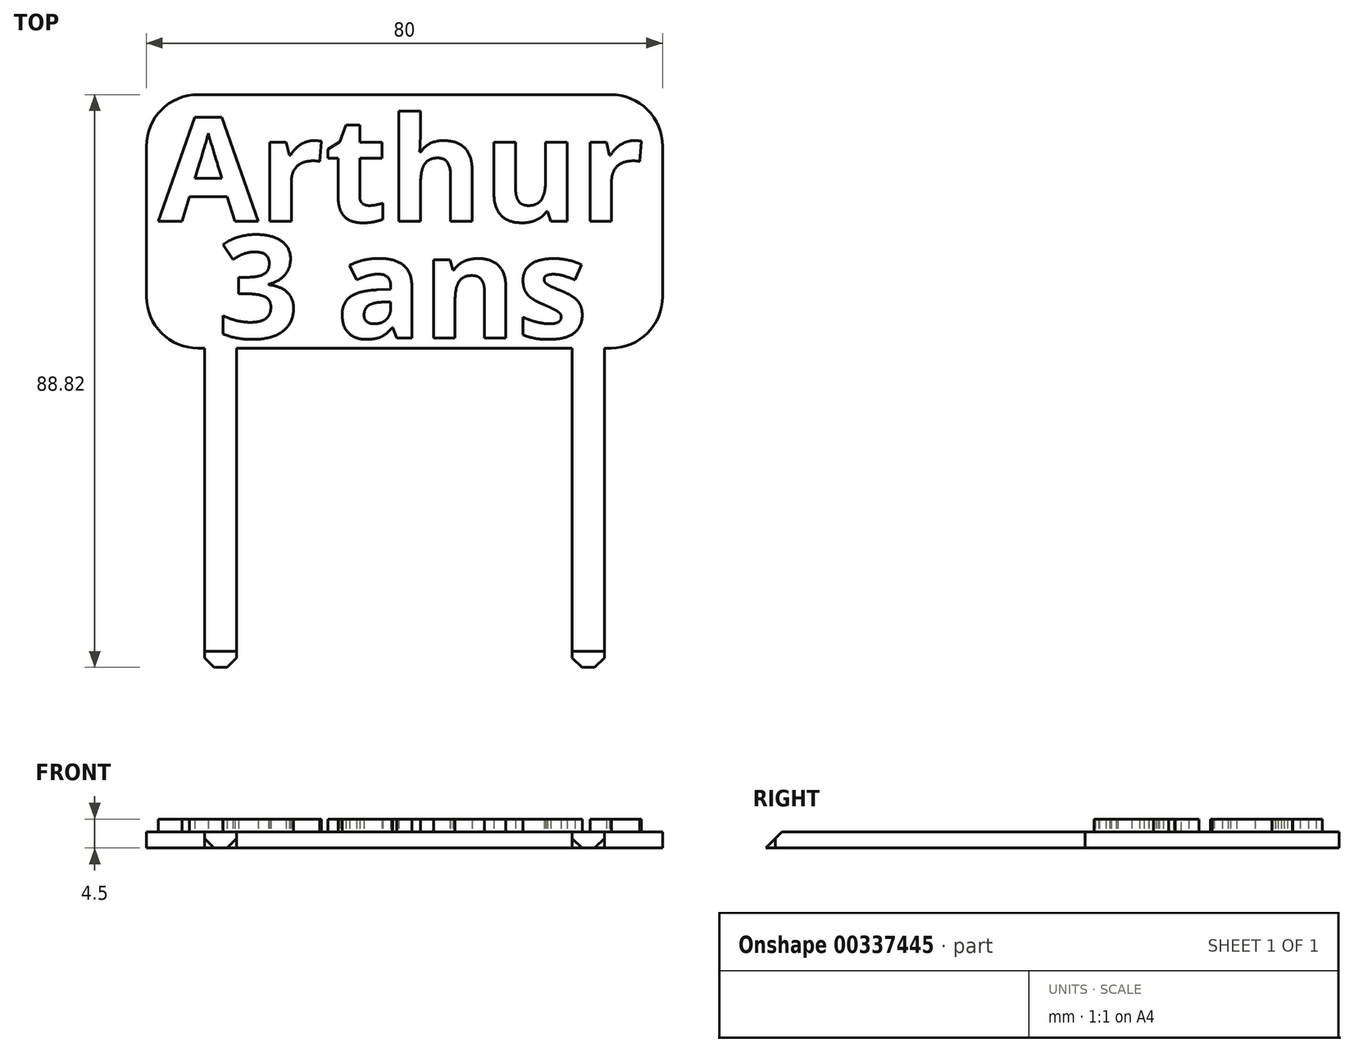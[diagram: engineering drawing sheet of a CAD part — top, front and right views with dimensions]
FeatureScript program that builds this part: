
annotation { "Feature Type Name" : "Feature", "Feature Type Description" : "" }
export const myFeature = defineFeature(function(context is Context, id is Id, definition is map)
    precondition{}
    {
        {
            var Q0;
            Q0=qCreatedBy(makeId("Top.planeOp"),FACE);
            var sketch = newSketch(context, id + "F0", { "sketchPlane" : qUnion([Q0])});
            skLineSegment(sketch, "E0.bottom", {"start": v(-40, 19.66) * mm, "end": v(40, 19.66) * mm});
            skLineSegment(sketch, "E0.top", {"start": v(-40, -19.66) * mm, "end": v(40, -19.66) * mm});
            skLineSegment(sketch, "E0.left", {"start": v(-40, 19.66) * mm, "end": v(-40, -19.66) * mm});
            skLineSegment(sketch, "E0.right", {"start": v(40, 19.66) * mm, "end": v(40, -19.66) * mm});
            skSolve(sketch);
        }
        {
            var Q0;
            Q0 = qSketchRegion(id + "F0", true);
            extrude(context, id + "F1", {"entities" : qUnion([Q0]), "depth" : 2.5 * mm});
        }
        {
            var Q0;
            Q0=makeQuery(id+"F1.opExtrude","CAP_FACE",FACE,{"disambiguationData":[OSD([sQuery(id+"F0.wireOp",EDGE,"E0.bottom"),sQuery(id+"F0.wireOp",EDGE,"E0.top"),sQuery(id+"F0.wireOp",EDGE,"E0.left"),sQuery(id+"F0.wireOp",EDGE,"E0.right")])],"isStart":false});
            var sketch = newSketch(context, id + "F2", { "sketchPlane" : qUnion([Q0])});
            skText(sketch, "E1", { "text": "Arthur", "fontName": "OpenSans-Bold.ttf"});
            skText(sketch, "E2", { "text": "3 ans", "fontName": "OpenSans-Bold.ttf"});
            const initialGuessF2  = {"E1": [-0.03818, 0, 1, 0, 0.01622], "E2": [-0.029, -0.01808, 1, 0, 0.01596]};
            skSetInitialGuess(sketch, initialGuessF2);
            skSolve(sketch);
        }
        {
            var Q0;
            Q0 = qSketchRegion(id + "F2", true);
            extrude(context, id + "F3", {"entities" : qUnion([Q0]), "operationType" : NewBodyOperationType.ADD, "depth" : 2 * mm});
        }
        {
            var Q0;
            Q0=qCreatedBy(makeId("Top.planeOp"),FACE);
            var sketch = newSketch(context, id + "F4", { "sketchPlane" : qUnion([Q0])});
            skLineSegment(sketch, "E3.bottom", {"start": v(-31, -69.66) * mm, "end": v(-26, -69.66) * mm});
            skLineSegment(sketch, "E3.top", {"start": v(-31, -19.66) * mm, "end": v(-26, -19.66) * mm});
            skLineSegment(sketch, "E3.left", {"start": v(-31, -69.66) * mm, "end": v(-31, -19.66) * mm});
            skLineSegment(sketch, "E3.right", {"start": v(-26, -69.66) * mm, "end": v(-26, -19.66) * mm});
            skLineSegment(sketch, "E4.MirrorCS", {"start": v(26, -69.66) * mm, "end": v(26, -19.66) * mm});
            skLineSegment(sketch, "E5.MirrorCS", {"start": v(31, -69.66) * mm, "end": v(26, -69.66) * mm});
            skLineSegment(sketch, "E6.MirrorCS", {"start": v(31, -69.66) * mm, "end": v(31, -19.66) * mm});
            skLineSegment(sketch, "E7.MirrorCS", {"start": v(31, -19.66) * mm, "end": v(26, -19.66) * mm});
            skSolve(sketch);
        }
        {
            var Q0;
            Q0 = qSketchRegion(id + "F4", true);
            extrude(context, id + "F5", {"entities" : qUnion([Q0]), "operationType" : NewBodyOperationType.ADD, "depth" : 2.5 * mm});
        }
        {
            var Q0;
            Q0=makeQuery(id+"F1.opExtrude","SWEPT_EDGE",EDGE,{"disambiguationData":[OSD([sQuery(id+"F0.wireOp",EDGE,"E0.top"),sQuery(id+"F0.wireOp",EDGE,"E0.right")])]});
            var Q1;
            Q1=makeQuery(id+"F1.opExtrude","SWEPT_EDGE",EDGE,{"disambiguationData":[OSD([sQuery(id+"F0.wireOp",EDGE,"E0.bottom"),sQuery(id+"F0.wireOp",EDGE,"E0.right")])]});
            var Q2;
            Q2=makeQuery(id+"F1.opExtrude","SWEPT_EDGE",EDGE,{"disambiguationData":[OSD([sQuery(id+"F0.wireOp",EDGE,"E0.top"),sQuery(id+"F0.wireOp",EDGE,"E0.left")])]});
            var Q3;
            Q3=makeQuery(id+"F1.opExtrude","SWEPT_EDGE",EDGE,{"disambiguationData":[OSD([sQuery(id+"F0.wireOp",EDGE,"E0.bottom"),sQuery(id+"F0.wireOp",EDGE,"E0.left")])]});
            fillet(context, id + "F6", {"entities" : qUnion([Q0, Q1, Q2, Q3]), "radius" : 8 * mm, "tangentPropagation" : true, "allowEdgeOverflow" : false});
        }
        {
            var Q0;
            Q0=makeQuery(id+"F5.opExtrude","SWEPT_EDGE",EDGE,{"disambiguationData":[OSD([sQuery(id+"F4.wireOp",EDGE,"E3.bottom"),sQuery(id+"F4.wireOp",EDGE,"E3.left")])]});
            var Q1;
            Q1=makeQuery(id+"F5.opExtrude","SWEPT_EDGE",EDGE,{"disambiguationData":[OSD([sQuery(id+"F4.wireOp",EDGE,"E3.bottom"),sQuery(id+"F4.wireOp",EDGE,"E3.right")])]});
            var Q2;
            Q2=makeQuery(id+"F5.opExtrude","SWEPT_EDGE",EDGE,{"disambiguationData":[OSD([sQuery(id+"F4.wireOp",EDGE,"E4.MirrorCS"),sQuery(id+"F4.wireOp",EDGE,"E5.MirrorCS")])]});
            var Q3;
            Q3=makeQuery(id+"F5.opExtrude","SWEPT_EDGE",EDGE,{"disambiguationData":[OSD([sQuery(id+"F4.wireOp",EDGE,"E5.MirrorCS"),sQuery(id+"F4.wireOp",EDGE,"E6.MirrorCS")])]});
            chamfer(context, id + "F7", {"entities" : qUnion([Q0, Q1, Q2, Q3]), "width" : 2 * mm, "tangentPropagation" : true});
        }
        {
            var Q0;
            Q0=makeQuery(id+"F5.opExtrude","CAP_EDGE",EDGE,{"disambiguationData":[OSD([sQuery(id+"F4.wireOp",EDGE,"E3.bottom")])],"isStart":false});
            var Q1;
            Q1=makeQuery(id+"F5.opExtrude","CAP_EDGE",EDGE,{"disambiguationData":[OSD([sQuery(id+"F4.wireOp",EDGE,"E5.MirrorCS")])],"isStart":false});
            chamfer(context, id + "F8", {"entities" : qUnion([Q0, Q1]), "width" : 3 * mm, "tangentPropagation" : true});
        }
    });
